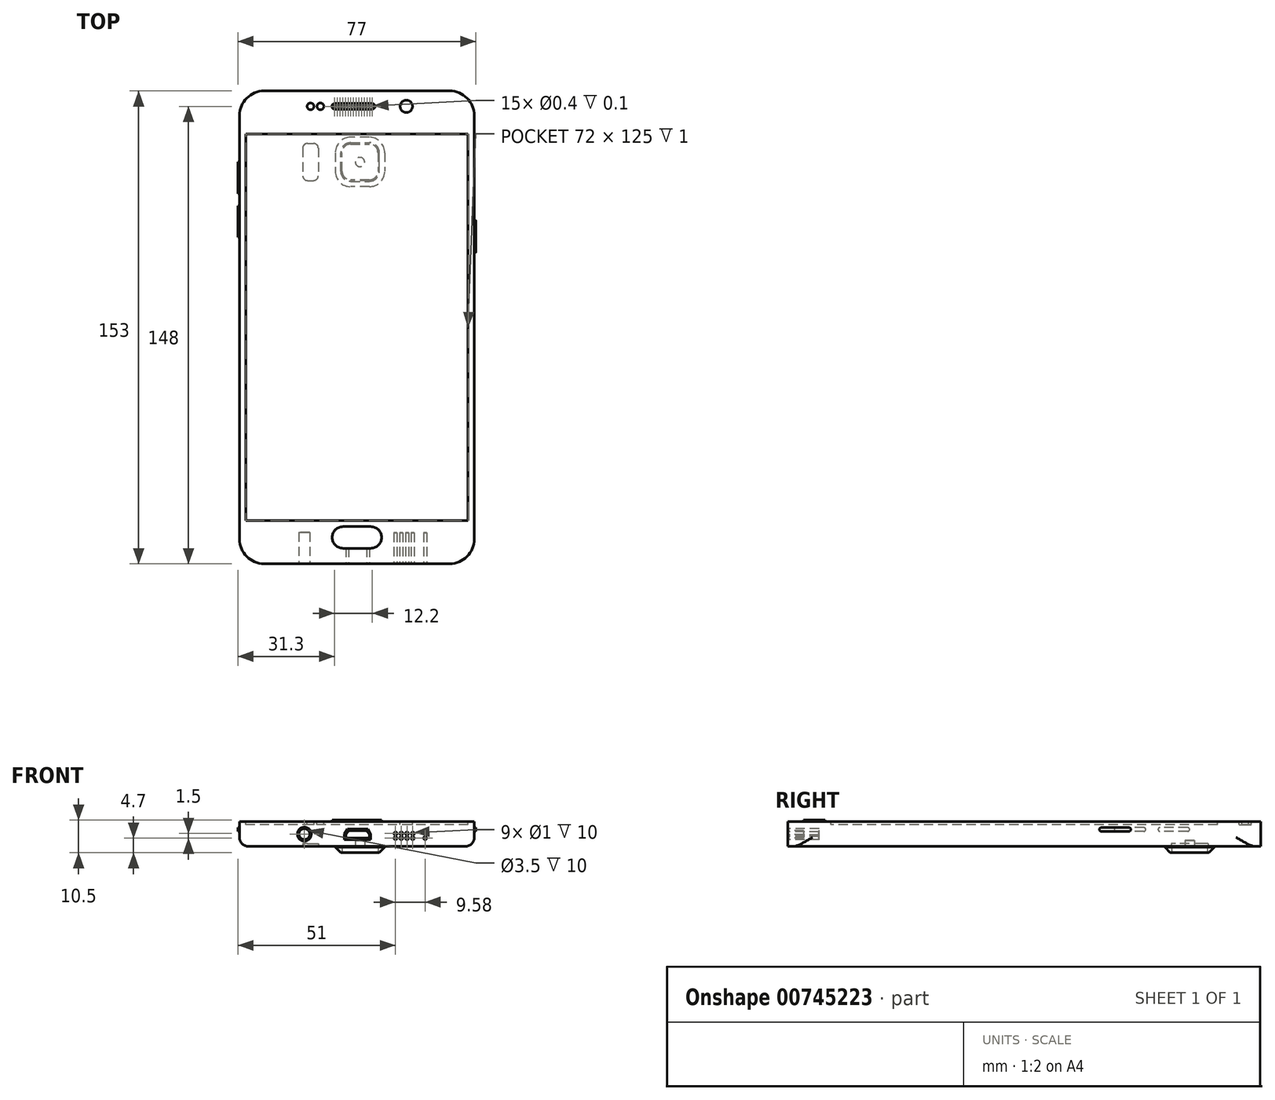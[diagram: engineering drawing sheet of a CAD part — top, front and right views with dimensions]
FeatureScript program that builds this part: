
annotation { "Feature Type Name" : "Feature", "Feature Type Description" : "" }
export const myFeature = defineFeature(function(context is Context, id is Id, definition is map)
    precondition{}
    {
        {
            var Q0;
            Q0=qCreatedBy(makeId("Top.planeOp"),FACE);
            var sketch = newSketch(context, id + "F0", { "sketchPlane" : qUnion([Q0])});
            skLineSegment(sketch, "E0.bottom", {"start": v(-38, 76.5) * mm, "end": v(38, 76.5) * mm});
            skLineSegment(sketch, "E0.top", {"start": v(-38, -76.5) * mm, "end": v(38, -76.5) * mm});
            skLineSegment(sketch, "E0.left", {"start": v(-38, 76.5) * mm, "end": v(-38, -76.5) * mm});
            skLineSegment(sketch, "E0.right", {"start": v(38, 76.5) * mm, "end": v(38, -76.5) * mm});
            skPoint(sketch, "E0.middle", {"position": v(0, 0) * mm});
            skLineSegment(sketch, "E1", {"start": v(0, 124.35) * mm, "end": v(0, -125.9) * mm, "construction": true});
            skLineSegment(sketch, "E2", {"start": v(-131.6, 0) * mm, "end": v(160.08, 0) * mm, "construction": true});
            skSolve(sketch);
        }
        {
            var Q0;
            Q0 = qSketchRegion(id + "F0", true);
            extrude(context, id + "F1", {"entities" : qUnion([Q0]), "depth" : 8 * mm, "offsetDistance" : 25 * mm});
        }
        {
            var Q0;
            Q0=makeQuery(id+"F1.opExtrude","CAP_FACE",FACE,{"disambiguationData":[OSD([sQuery(id+"F0.wireOp",EDGE,"E0.bottom"),sQuery(id+"F0.wireOp",EDGE,"E0.top"),sQuery(id+"F0.wireOp",EDGE,"E0.left"),sQuery(id+"F0.wireOp",EDGE,"E0.right")])],"isStart":false});
            var sketch = newSketch(context, id + "F2", { "sketchPlane" : qUnion([Q0])});
            skLineSegment(sketch, "E3.bottom", {"start": v(36, 62.5) * mm, "end": v(-36, 62.5) * mm});
            skLineSegment(sketch, "E3.top", {"start": v(36, -62.5) * mm, "end": v(-36, -62.5) * mm});
            skLineSegment(sketch, "E3.left", {"start": v(36, 62.5) * mm, "end": v(36, -62.5) * mm});
            skLineSegment(sketch, "E3.right", {"start": v(-36, 62.5) * mm, "end": v(-36, -62.5) * mm});
            skPoint(sketch, "E3.middle", {"position": v(0, 0) * mm});
            skSolve(sketch);
        }
        {
            var Q0;
            Q0=makeQuery(id+"F2.imprint","IMPRINT",FACE,{"disambiguationData":[TD([[makeQuery(id+"F2.imprint","IMPRINT",EDGE,{"derivedFrom":sQuery(id+"F2.wireOp",EDGE,"E3.bottom")}),1.0]])]});
            extrude(context, id + "F3", {"entities" : qUnion([Q0]), "operationType" : NewBodyOperationType.REMOVE, "oppositeDirection" : true, "depth" : 1 * mm, "offsetDistance" : 25 * mm});
        }
        {
            var Q0;
            Q0=makeQuery(id+"F1.opExtrude","CAP_FACE",FACE,{"disambiguationData":[OSD([sQuery(id+"F0.wireOp",EDGE,"E0.bottom"),sQuery(id+"F0.wireOp",EDGE,"E0.top"),sQuery(id+"F0.wireOp",EDGE,"E0.left"),sQuery(id+"F0.wireOp",EDGE,"E0.right")])],"isStart":false});
            var sketch = newSketch(context, id + "F4", { "sketchPlane" : qUnion([Q0])});
            skArc(sketch, "E4", {"start": v(-4.5, -64.5) * mm, "mid": v(-8, -68) * mm, "end": v(-4.5, -71.5) * mm});
            skArc(sketch, "E5", {"start": v(4.5, -71.5) * mm, "mid": v(8, -68) * mm, "end": v(4.5, -64.5) * mm});
            skLineSegment(sketch, "E6", {"start": v(-4.5, 87.17) * mm, "end": v(-4.5, -115.27) * mm, "construction": true});
            skLineSegment(sketch, "E7", {"start": v(4.5, 87.92) * mm, "end": v(4.5, -126.27) * mm, "construction": true});
            skLineSegment(sketch, "E8", {"start": v(-4.5, -64.5) * mm, "end": v(4.5, -64.5) * mm});
            skLineSegment(sketch, "E9", {"start": v(-4.5, -71.5) * mm, "end": v(4.5, -71.5) * mm});
            skSolve(sketch);
        }
        {
            var Q0;
            Q0 = qSketchRegion(id + "F4", true);
            extrude(context, id + "F5", {"entities" : qUnion([Q0]), "operationType" : NewBodyOperationType.ADD, "depth" : .5 * mm, "offsetDistance" : 25 * mm});
        }
        {
            var Q0;
            Q0=makeQuery(id+"F1.opExtrude","CAP_FACE",FACE,{"disambiguationData":[OSD([sQuery(id+"F0.wireOp",EDGE,"E0.bottom"),sQuery(id+"F0.wireOp",EDGE,"E0.top"),sQuery(id+"F0.wireOp",EDGE,"E0.left"),sQuery(id+"F0.wireOp",EDGE,"E0.right")])],"isStart":false});
            var sketch = newSketch(context, id + "F6", { "sketchPlane" : qUnion([Q0])});
            skCircle(sketch, "E10", {"center": v(-15, 71.5) * mm, "radius": 1.1 * mm});
            skCircle(sketch, "E11", {"center": v(-11.8, 71.5) * mm, "radius": 1.1 * mm});
            skLineSegment(sketch, "E12", {"start": v(-15, 71.5) * mm, "end": v(-11.8, 71.5) * mm, "construction": true});
            skCircle(sketch, "E13", {"center": v(16, 71.5) * mm, "radius": 2 * mm});
            skLineSegment(sketch, "E14", {"start": v(-11.8, 71.5) * mm, "end": v(16, 71.5) * mm, "construction": true});
            skSolve(sketch);
        }
        {
            var Q0;
            Q0=makeQuery(id+"F6.imprint","IMPRINT",FACE,{"disambiguationData":[TD([[makeQuery(id+"F6.imprint","IMPRINT",EDGE,{"derivedFrom":sQuery(id+"F6.wireOp",EDGE,"E10")}),1.0]])]});
            var Q1;
            Q1=makeQuery(id+"F6.imprint","IMPRINT",FACE,{"disambiguationData":[TD([[makeQuery(id+"F6.imprint","IMPRINT",EDGE,{"derivedFrom":sQuery(id+"F6.wireOp",EDGE,"E11")}),1.0]])]});
            var Q2;
            Q2=makeQuery(id+"F6.imprint","IMPRINT",FACE,{"disambiguationData":[TD([[makeQuery(id+"F6.imprint","IMPRINT",EDGE,{"derivedFrom":sQuery(id+"F6.wireOp",EDGE,"E13")}),1.0]])]});
            extrude(context, id + "F7", {"entities" : qUnion([Q0, Q1, Q2]), "operationType" : NewBodyOperationType.REMOVE, "oppositeDirection" : true, "depth" : 1 * mm, "offsetDistance" : 25 * mm});
        }
        {
            var Q0;
            Q0=makeQuery(id+"F1.opExtrude","CAP_FACE",FACE,{"disambiguationData":[OSD([sQuery(id+"F0.wireOp",EDGE,"E0.bottom"),sQuery(id+"F0.wireOp",EDGE,"E0.top"),sQuery(id+"F0.wireOp",EDGE,"E0.left"),sQuery(id+"F0.wireOp",EDGE,"E0.right")])],"isStart":false});
            var sketch = newSketch(context, id + "F8", { "sketchPlane" : qUnion([Q0])});
            skArc(sketch, "E15", {"start": v(-7.2, 72.4) * mm, "mid": v(-8.1, 71.5) * mm, "end": v(-7.2, 70.6) * mm});
            skArc(sketch, "E16", {"start": v(5, 70.6) * mm, "mid": v(5.9, 71.5) * mm, "end": v(5, 72.4) * mm});
            skLineSegment(sketch, "E17", {"start": v(-7.2, 72.4) * mm, "end": v(5, 72.4) * mm});
            skLineSegment(sketch, "E18", {"start": v(-7.2, 70.6) * mm, "end": v(5, 70.6) * mm});
            skSolve(sketch);
        }
        {
            var Q0;
            Q0 = qSketchRegion(id + "F8", true);
            extrude(context, id + "F9", {"entities" : qUnion([Q0]), "operationType" : NewBodyOperationType.ADD, "depth" : 0.01 * mm, "offsetDistance" : 25 * mm});
        }
        {
            var Q0;
            Q0=makeQuery(id+"F9.opExtrude","CAP_FACE",FACE,{"disambiguationData":[OSD([sQuery(id+"F8.wireOp",EDGE,"E15"),sQuery(id+"F8.wireOp",EDGE,"E16"),sQuery(id+"F8.wireOp",EDGE,"E17"),sQuery(id+"F8.wireOp",EDGE,"E18")])],"isStart":false});
            var sketch = newSketch(context, id + "F10", { "sketchPlane" : qUnion([Q0])});
            skLineSegment(sketch, "E19", {"start": v(-7.2, 71.5) * mm, "end": v(5, 71.5) * mm, "construction": true});
            skLineSegment(sketch, "E20", {"start": v(-1.1, 79.57) * mm, "end": v(-1.1, 67.09) * mm, "construction": true});
            skCircle(sketch, "E21", {"center": v(-1.1, 71.5) * mm, "radius": 0.2 * mm});
            skCircle(sketch, "E22", {"center": v(-7.2, 71.5) * mm, "radius": 0.2 * mm});
            skCircle(sketch, "E23", {"center": v(5, 71.5) * mm, "radius": 0.2 * mm});
            skCircle(sketch, "E24", {"center": v(-6.33, 71.5) * mm, "radius": 0.2 * mm});
            skCircle(sketch, "E25", {"center": v(-5.46, 71.5) * mm, "radius": 0.2 * mm});
            skCircle(sketch, "E26", {"center": v(-4.59, 71.5) * mm, "radius": 0.2 * mm});
            skCircle(sketch, "E27", {"center": v(-3.7, 71.5) * mm, "radius": 0.2 * mm});
            skCircle(sketch, "E28", {"center": v(-2.84, 71.5) * mm, "radius": 0.2 * mm});
            skCircle(sketch, "E29", {"center": v(-1.97, 71.5) * mm, "radius": 0.2 * mm});
            skCircle(sketch, "E30", {"center": v(-0.23, 71.5) * mm, "radius": 0.2 * mm});
            skCircle(sketch, "E31", {"center": v(0.64, 71.5) * mm, "radius": 0.2 * mm});
            skCircle(sketch, "E32", {"center": v(1.51, 71.5) * mm, "radius": 0.2 * mm});
            skCircle(sketch, "E33", {"center": v(2.39, 71.5) * mm, "radius": 0.2 * mm});
            skCircle(sketch, "E34", {"center": v(3.26, 71.5) * mm, "radius": 0.2 * mm});
            skCircle(sketch, "E35", {"center": v(4.13, 71.5) * mm, "radius": 0.2 * mm});
            skSolve(sketch);
        }
        {
            var Q0;
            Q0 = qSketchRegion(id + "F10", true);
            extrude(context, id + "F11", {"entities" : qUnion([Q0]), "operationType" : NewBodyOperationType.REMOVE, "oppositeDirection" : true, "depth" : .1 * mm, "offsetDistance" : 25 * mm});
        }
        {
            var Q0;
            Q0=makeQuery(id+"F1.opExtrude","SWEPT_FACE",FACE,{"disambiguationData":[OSD([sQuery(id+"F0.wireOp",EDGE,"E0.left")])]});
            var sketch = newSketch(context, id + "F12", { "sketchPlane" : qUnion([Q0])});
            skArc(sketch, "E36", {"start": v(-52.9, 6.1) * mm, "mid": v(-53.5, 5.5) * mm, "end": v(-52.9, 4.9) * mm});
            skArc(sketch, "E37", {"start": v(-43.9, 4.9) * mm, "mid": v(-43.3, 5.5) * mm, "end": v(-43.9, 6.1) * mm});
            skArc(sketch, "E38", {"start": v(-38.7, 6.1) * mm, "mid": v(-39.3, 5.5) * mm, "end": v(-38.7, 4.9) * mm});
            skArc(sketch, "E39", {"start": v(-29.7, 4.9) * mm, "mid": v(-29.1, 5.5) * mm, "end": v(-29.7, 6.1) * mm});
            skLineSegment(sketch, "E40", {"start": v(-52.9, 5.5) * mm, "end": v(-29.7, 5.5) * mm, "construction": true});
            skLineSegment(sketch, "E41", {"start": v(-52.9, 6.1) * mm, "end": v(-43.9, 6.1) * mm});
            skLineSegment(sketch, "E42", {"start": v(-52.9, 4.9) * mm, "end": v(-43.9, 4.9) * mm});
            skLineSegment(sketch, "E43.trimOffspring", {"start": v(-38.7, 6.1) * mm, "end": v(-29.7, 6.1) * mm});
            skLineSegment(sketch, "E44.trimOffspring", {"start": v(-38.7, 4.9) * mm, "end": v(-29.7, 4.9) * mm});
            skSolve(sketch);
        }
        {
            var Q0;
            Q0 = qSketchRegion(id + "F12", true);
            extrude(context, id + "F13", {"entities" : qUnion([Q0]), "operationType" : NewBodyOperationType.ADD, "depth" : .5 * mm, "offsetDistance" : 25 * mm});
        }
        {
            var Q0;
            Q0=makeQuery(id+"F1.opExtrude","SWEPT_FACE",FACE,{"disambiguationData":[OSD([sQuery(id+"F0.wireOp",EDGE,"E0.right")])]});
            var sketch = newSketch(context, id + "F14", { "sketchPlane" : qUnion([Q0])});
            skCircle(sketch, "E45", {"center": v(24.9, 5.5) * mm, "radius": 0.6 * mm});
            skCircle(sketch, "E46", {"center": v(33.9, 5.5) * mm, "radius": 0.6 * mm});
            skLineSegment(sketch, "E47", {"start": v(24.9, 6.1) * mm, "end": v(33.9, 6.1) * mm});
            skLineSegment(sketch, "E48", {"start": v(24.9, 4.9) * mm, "end": v(33.9, 4.9) * mm});
            skLineSegment(sketch, "E49", {"start": v(24.9, 5.5) * mm, "end": v(33.9, 5.5) * mm, "construction": true});
            skSolve(sketch);
        }
        {
            var Q0;
            Q0 = qSketchRegion(id + "F14", true);
            extrude(context, id + "F15", {"entities" : qUnion([Q0]), "operationType" : NewBodyOperationType.ADD, "depth" : .5 * mm, "offsetDistance" : 25 * mm});
        }
        {
            var Q0;
            Q0=makeQuery(id+"F1.opExtrude","SWEPT_FACE",FACE,{"disambiguationData":[OSD([sQuery(id+"F0.wireOp",EDGE,"E0.top")])]});
            var sketch = newSketch(context, id + "F16", { "sketchPlane" : qUnion([Q0])});
            skCircle(sketch, "E50", {"center": v(-17, 4) * mm, "radius": 2.25 * mm});
            skSolve(sketch);
        }
        {
            var Q0;
            Q0 = qSketchRegion(id + "F16", true);
            extrude(context, id + "F17", {"entities" : qUnion([Q0]), "operationType" : NewBodyOperationType.REMOVE, "oppositeDirection" : true, "depth" : .1 * mm, "offsetDistance" : 25 * mm});
        }
        {
            var Q0;
            Q0=makeQuery(id+"F17.boolean.opBoolean","COPY",FACE,{"derivedFrom":makeQuery(id+"F17.opExtrude","CAP_FACE",FACE,{"disambiguationData":[OSD([sQuery(id+"F16.wireOp",EDGE,"E50")])],"isStart":false})});
            var sketch = newSketch(context, id + "F18", { "sketchPlane" : qUnion([Q0])});
            skCircle(sketch, "E51", {"center": v(-17, 4) * mm, "radius": 1.75 * mm});
            skSolve(sketch);
        }
        {
            var Q0;
            Q0 = qSketchRegion(id + "F18", true);
            extrude(context, id + "F19", {"entities" : qUnion([Q0]), "operationType" : NewBodyOperationType.REMOVE, "oppositeDirection" : true, "depth" : 10 * mm, "offsetDistance" : 25 * mm});
        }
        {
            var Q0;
            Q0=makeQuery(id+"F1.opExtrude","SWEPT_FACE",FACE,{"disambiguationData":[OSD([sQuery(id+"F0.wireOp",EDGE,"E0.top")])]});
            var sketch = newSketch(context, id + "F20", { "sketchPlane" : qUnion([Q0])});
            skLineSegment(sketch, "E52", {"start": v(0.25, -5.5) * mm, "end": v(0.25, -17.35) * mm, "construction": true});
            skLineSegment(sketch, "E53", {"start": v(0.25, 5.6) * mm, "end": v(3.5, 5.6) * mm});
            skLineSegment(sketch, "E54", {"start": v(3.5, 5.6) * mm, "end": v(4.5, 4) * mm});
            skLineSegment(sketch, "E55", {"start": v(4.5, 4) * mm, "end": v(4.5, 2.2) * mm});
            skLineSegment(sketch, "E56", {"start": v(4.5, 2.2) * mm, "end": v(0.25, 2.2) * mm});
            skLineSegment(sketch, "E57.MirrorCS", {"start": v(-4, 2.2) * mm, "end": v(0.25, 2.2) * mm});
            skLineSegment(sketch, "E58.MirrorCS", {"start": v(-4, 4) * mm, "end": v(-4, 2.2) * mm});
            skLineSegment(sketch, "E59.MirrorCS", {"start": v(-3, 5.6) * mm, "end": v(-4, 4) * mm});
            skLineSegment(sketch, "E60.MirrorCS", {"start": v(0.25, 5.6) * mm, "end": v(-3, 5.6) * mm});
            skLineSegment(sketch, "E61", {"start": v(-4, 4) * mm, "end": v(36.69, 4) * mm, "construction": true});
            skSolve(sketch);
        }
        {
            var Q0;
            Q0 = qSketchRegion(id + "F20", true);
            extrude(context, id + "F21", {"entities" : qUnion([Q0]), "operationType" : NewBodyOperationType.REMOVE, "oppositeDirection" : true, "depth" : .1 * mm, "offsetDistance" : 25 * mm});
        }
        {
            var Q0;
            Q0=makeQuery(id+"F21.boolean.opBoolean","COPY",FACE,{"derivedFrom":makeQuery(id+"F21.opExtrude","CAP_FACE",FACE,{"disambiguationData":[OSD([sQuery(id+"F20.wireOp",EDGE,"E53"),sQuery(id+"F20.wireOp",EDGE,"E54"),sQuery(id+"F20.wireOp",EDGE,"E55"),sQuery(id+"F20.wireOp",EDGE,"E56"),sQuery(id+"F20.wireOp",EDGE,"E57.MirrorCS"),sQuery(id+"F20.wireOp",EDGE,"E58.MirrorCS"),sQuery(id+"F20.wireOp",EDGE,"E59.MirrorCS"),sQuery(id+"F20.wireOp",EDGE,"E60.MirrorCS")])],"isStart":false})});
            var sketch = newSketch(context, id + "F22", { "sketchPlane" : qUnion([Q0])});
            skLineSegment(sketch, "E62", {"start": v(0.25, 7.04) * mm, "end": v(0.25, -1.36) * mm, "construction": true});
            skPoint(sketch, "E62.startSnap0", {"position": v(0.25, 5.6) * mm});
            skLineSegment(sketch, "E63", {"start": v(0.25, 5.1) * mm, "end": v(3.22, 5.1) * mm});
            skLineSegment(sketch, "E64", {"start": v(3.22, 5.1) * mm, "end": v(4, 3.86) * mm});
            skLineSegment(sketch, "E65", {"start": v(4, 3.86) * mm, "end": v(4, 2.7) * mm});
            skLineSegment(sketch, "E66", {"start": v(4, 2.7) * mm, "end": v(0.25, 2.7) * mm});
            skLineSegment(sketch, "E67.MirrorCS", {"start": v(-3.5, 2.7) * mm, "end": v(0.25, 2.7) * mm});
            skLineSegment(sketch, "E68.MirrorCS", {"start": v(0.25, 5.1) * mm, "end": v(-2.72, 5.1) * mm});
            skLineSegment(sketch, "E69.MirrorCS", {"start": v(-2.72, 5.1) * mm, "end": v(-3.5, 3.86) * mm});
            skLineSegment(sketch, "E70.MirrorCS", {"start": v(-3.5, 3.86) * mm, "end": v(-3.5, 2.7) * mm});
            skSolve(sketch);
        }
        {
            var Q0;
            Q0 = qSketchRegion(id + "F22", true);
            extrude(context, id + "F23", {"entities" : qUnion([Q0]), "operationType" : NewBodyOperationType.REMOVE, "oppositeDirection" : true, "depth" : 5 * mm, "offsetDistance" : 25 * mm});
        }
        {
            var Q0;
            Q0=makeQuery(id+"F1.opExtrude","SWEPT_FACE",FACE,{"disambiguationData":[OSD([sQuery(id+"F0.wireOp",EDGE,"E0.top")])]});
            var sketch = newSketch(context, id + "F24", { "sketchPlane" : qUnion([Q0])});
            skLineSegment(sketch, "E71", {"start": v(44.86, 3.45) * mm, "end": v(6.77, 3.45) * mm, "construction": true});
            skLineSegment(sketch, "E72", {"start": v(12.5, 10.5) * mm, "end": v(12.5, -4.17) * mm, "construction": true});
            skLineSegment(sketch, "E73.0", {"start": v(44.86, 4.2) * mm, "end": v(6.77, 4.2) * mm, "construction": true});
            skLineSegment(sketch, "E74.0", {"start": v(44.86, 2.7) * mm, "end": v(6.77, 2.7) * mm, "construction": true});
            skLineSegment(sketch, "E75.0", {"start": v(-43, -5) * mm, "end": v(43, -5) * mm, "construction": true});
            skLineSegment(sketch, "E75.1", {"start": v(-43, 13) * mm, "end": v(-43, -5) * mm, "construction": true});
            skLineSegment(sketch, "E75.2", {"start": v(43, 13) * mm, "end": v(-43, 13) * mm, "construction": true});
            skLineSegment(sketch, "E75.3", {"start": v(43, -5) * mm, "end": v(43, 13) * mm, "construction": true});
            skLineSegment(sketch, "E76.0", {"start": v(14.36, 10.5) * mm, "end": v(14.36, -4.17) * mm, "construction": true});
            skLineSegment(sketch, "E77.0", {"start": v(16.22, 10.5) * mm, "end": v(16.22, -4.17) * mm, "construction": true});
            skLineSegment(sketch, "E78.0", {"start": v(18.08, 10.5) * mm, "end": v(18.08, -4.17) * mm, "construction": true});
            skCircle(sketch, "E79", {"center": v(12.5, 4.2) * mm, "radius": 0.5 * mm});
            skCircle(sketch, "E80", {"center": v(14.36, 4.2) * mm, "radius": 0.5 * mm});
            skCircle(sketch, "E81", {"center": v(16.22, 4.2) * mm, "radius": 0.5 * mm});
            skCircle(sketch, "E82", {"center": v(18.08, 4.2) * mm, "radius": 0.5 * mm});
            skCircle(sketch, "E83", {"center": v(18.08, 2.7) * mm, "radius": 0.5 * mm});
            skCircle(sketch, "E84", {"center": v(16.22, 2.7) * mm, "radius": 0.5 * mm});
            skCircle(sketch, "E85", {"center": v(14.36, 2.7) * mm, "radius": 0.5 * mm});
            skCircle(sketch, "E86", {"center": v(12.5, 2.7) * mm, "radius": 0.5 * mm});
            skLineSegment(sketch, "E87", {"start": v(22.08, 10.5) * mm, "end": v(22.08, -2.74) * mm, "construction": true});
            skCircle(sketch, "E88", {"center": v(22.08, 2.7) * mm, "radius": 0.5 * mm});
            skSolve(sketch);
        }
        {
            var Q0;
            Q0 = qSketchRegion(id + "F24", true);
            extrude(context, id + "F25", {"entities" : qUnion([Q0]), "operationType" : NewBodyOperationType.REMOVE, "oppositeDirection" : true, "depth" : 10 * mm, "offsetDistance" : 25 * mm});
        }
        {
            var Q0;
            Q0=makeQuery(id+"F1.opExtrude","CAP_FACE",FACE,{"disambiguationData":[OSD([sQuery(id+"F0.wireOp",EDGE,"E0.bottom"),sQuery(id+"F0.wireOp",EDGE,"E0.top"),sQuery(id+"F0.wireOp",EDGE,"E0.left"),sQuery(id+"F0.wireOp",EDGE,"E0.right")])],"isStart":true});
            var sketch = newSketch(context, id + "F26", { "sketchPlane" : qUnion([Q0])});
            skLineSegment(sketch, "E89.bottom", {"start": v(4, -61.5) * mm, "end": v(-2, -61.5) * mm});
            skLineSegment(sketch, "E89.top", {"start": v(4, -45.5) * mm, "end": v(-2, -45.5) * mm});
            skLineSegment(sketch, "E89.left", {"start": v(9, -56.5) * mm, "end": v(9, -50.5) * mm});
            skLineSegment(sketch, "E89.right", {"start": v(-7, -56.5) * mm, "end": v(-7, -50.5) * mm});
            skPoint(sketch, "E90.visualSharp", {"position": v(-7, -61.5) * mm});
            skArc(sketch, "E90.filletArc", {"start": v(-7, -56.5) * mm, "mid": v(-5.54, -60.04) * mm, "end": v(-2, -61.5) * mm});
            skPoint(sketch, "E91.visualSharp", {"position": v(9, -45.5) * mm});
            skArc(sketch, "E91.filletArc", {"start": v(9, -50.5) * mm, "mid": v(7.54, -46.96) * mm, "end": v(4, -45.5) * mm});
            skPoint(sketch, "E92.visualSharp", {"position": v(9, -61.5) * mm});
            skArc(sketch, "E92.filletArc", {"start": v(4, -61.5) * mm, "mid": v(7.54, -60.04) * mm, "end": v(9, -56.5) * mm});
            skPoint(sketch, "E93.visualSharp", {"position": v(-7, -45.5) * mm});
            skArc(sketch, "E93.filletArc", {"start": v(-2, -45.5) * mm, "mid": v(-5.54, -46.96) * mm, "end": v(-7, -50.5) * mm});
            skSolve(sketch);
        }
        {
            var Q0;
            Q0 = qSketchRegion(id + "F26", true);
            extrude(context, id + "F27", {"entities" : qUnion([Q0]), "operationType" : NewBodyOperationType.ADD, "depth" : 2 * mm, "offsetDistance" : 25 * mm});
        }
        {
            var Q0;
            Q0=makeQuery(id+"F27.opExtrude","CAP_EDGE",EDGE,{"disambiguationData":[OSD([sQuery(id+"F26.wireOp",EDGE,"E89.left")])],"isStart":false});
            chamfer(context, id + "F28", {"entities" : qUnion([Q0]), "width" : 1.8 * mm, "tangentPropagation" : true});
        }
        {
            var Q0;
            {var subQ0=sQuery(id+"F26.wireOp",EDGE,"E92.filletArc");Q0=makeQuery(id+"F28.opChamfer","BLEND_EDGE",EDGE,{"blendedFrom":[makeQuery(id+"F27.opExtrude","CAP_EDGE",EDGE,{"disambiguationData":[OSD([subQ0])],"isStart":false}),makeQuery(id+"F27.opExtrude","CAP_FACE",FACE,{"disambiguationData":[OSD([sQuery(id+"F26.wireOp",EDGE,"E89.bottom"),sQuery(id+"F26.wireOp",EDGE,"E89.top"),sQuery(id+"F26.wireOp",EDGE,"E89.left"),sQuery(id+"F26.wireOp",EDGE,"E89.right"),sQuery(id+"F26.wireOp",EDGE,"E90.filletArc"),sQuery(id+"F26.wireOp",EDGE,"E91.filletArc"),subQ0,sQuery(id+"F26.wireOp",EDGE,"E93.filletArc")])],"isStart":false})],"blendedInto":[makeQuery(id+"F27.opExtrude","CAP_FACE",FACE,{"disambiguationData":[OSD([sQuery(id+"F26.wireOp",EDGE,"E89.bottom"),sQuery(id+"F26.wireOp",EDGE,"E89.top"),sQuery(id+"F26.wireOp",EDGE,"E89.left"),sQuery(id+"F26.wireOp",EDGE,"E89.right"),sQuery(id+"F26.wireOp",EDGE,"E90.filletArc"),sQuery(id+"F26.wireOp",EDGE,"E91.filletArc"),subQ0,sQuery(id+"F26.wireOp",EDGE,"E93.filletArc")])],"isStart":false})]});}
            chamfer(context, id + "F29", {"entities" : qUnion([Q0]), "width" : 0.2 * mm, "tangentPropagation" : true});
        }
        {
            var Q0;
            Q0=makeQuery(id+"F27.opExtrude","CAP_FACE",FACE,{"disambiguationData":[OSD([sQuery(id+"F26.wireOp",EDGE,"E89.bottom"),sQuery(id+"F26.wireOp",EDGE,"E89.top"),sQuery(id+"F26.wireOp",EDGE,"E89.left"),sQuery(id+"F26.wireOp",EDGE,"E89.right"),sQuery(id+"F26.wireOp",EDGE,"E90.filletArc"),sQuery(id+"F26.wireOp",EDGE,"E91.filletArc"),sQuery(id+"F26.wireOp",EDGE,"E92.filletArc"),sQuery(id+"F26.wireOp",EDGE,"E93.filletArc")])],"isStart":false});
            var sketch = newSketch(context, id + "F30", { "sketchPlane" : qUnion([Q0])});
            skArc(sketch, "E94.0", {"start": v(-4.8, -56.5) * mm, "mid": v(-3.98, -58.48) * mm, "end": v(-2, -59.3) * mm});
            skLineSegment(sketch, "E94.1", {"start": v(-4.8, -50.5) * mm, "end": v(-4.8, -56.5) * mm});
            skLineSegment(sketch, "E94.2", {"start": v(-2, -59.3) * mm, "end": v(4, -59.3) * mm});
            skArc(sketch, "E94.3", {"start": v(-2, -47.7) * mm, "mid": v(-3.98, -48.52) * mm, "end": v(-4.8, -50.5) * mm});
            skArc(sketch, "E94.4", {"start": v(4, -59.3) * mm, "mid": v(5.98, -58.48) * mm, "end": v(6.8, -56.5) * mm});
            skLineSegment(sketch, "E94.5", {"start": v(6.8, -56.5) * mm, "end": v(6.8, -50.5) * mm});
            skArc(sketch, "E94.6", {"start": v(6.8, -50.5) * mm, "mid": v(5.98, -48.52) * mm, "end": v(4, -47.7) * mm});
            skLineSegment(sketch, "E94.7", {"start": v(4, -47.7) * mm, "end": v(-2, -47.7) * mm});
            skSolve(sketch);
        }
        {
            var Q0;
            Q0 = qSketchRegion(id + "F30", true);
            extrude(context, id + "F31", {"entities" : qUnion([Q0]), "operationType" : NewBodyOperationType.REMOVE, "oppositeDirection" : true, "depth" : 2 * mm, "offsetDistance" : 25 * mm});
        }
        {
            var Q0;
            Q0=makeQuery(id+"F31.boolean.opBoolean","COPY",FACE,{"derivedFrom":makeQuery(id+"F31.opExtrude","CAP_FACE",FACE,{"disambiguationData":[OSD([sQuery(id+"F30.wireOp",EDGE,"E94.0"),sQuery(id+"F30.wireOp",EDGE,"E94.1"),sQuery(id+"F30.wireOp",EDGE,"E94.2"),sQuery(id+"F30.wireOp",EDGE,"E94.3"),sQuery(id+"F30.wireOp",EDGE,"E94.4"),sQuery(id+"F30.wireOp",EDGE,"E94.5"),sQuery(id+"F30.wireOp",EDGE,"E94.6"),sQuery(id+"F30.wireOp",EDGE,"E94.7")])],"isStart":false})});
            var sketch = newSketch(context, id + "F32", { "sketchPlane" : qUnion([Q0])});
            skLineSegment(sketch, "E95", {"start": v(1, -59.3) * mm, "end": v(1, -47.7) * mm, "construction": true});
            skLineSegment(sketch, "E96", {"start": v(6.8, -53.5) * mm, "end": v(-4.8, -53.5) * mm, "construction": true});
            skCircle(sketch, "E97", {"center": v(1, -53.5) * mm, "radius": 1.5 * mm});
            skSolve(sketch);
        }
        {
            var Q0;
            Q0 = qSketchRegion(id + "F32", true);
            extrude(context, id + "F33", {"entities" : qUnion([Q0]), "operationType" : NewBodyOperationType.REMOVE, "oppositeDirection" : true, "depth" : 2 * mm, "offsetDistance" : 25 * mm});
        }
        {
            var Q0;
            Q0=makeQuery(id+"F1.opExtrude","CAP_FACE",FACE,{"disambiguationData":[OSD([sQuery(id+"F0.wireOp",EDGE,"E0.bottom"),sQuery(id+"F0.wireOp",EDGE,"E0.top"),sQuery(id+"F0.wireOp",EDGE,"E0.left"),sQuery(id+"F0.wireOp",EDGE,"E0.right")])],"isStart":true});
            var sketch = newSketch(context, id + "F34", { "sketchPlane" : qUnion([Q0])});
            skLineSegment(sketch, "E98", {"start": v(9, -53.5) * mm, "end": v(-43.1, -53.5) * mm, "construction": true});
            skLineSegment(sketch, "E99", {"start": v(-15, -78.99) * mm, "end": v(-15, -36.79) * mm, "construction": true});
            skLineSegment(sketch, "E100", {"start": v(-38, -70.47) * mm, "end": v(-38, -82.04) * mm, "construction": true});
            skLineSegment(sketch, "E101.bottom", {"start": v(-16, -59.5) * mm, "end": v(-14, -59.5) * mm});
            skLineSegment(sketch, "E101.top", {"start": v(-16, -47.5) * mm, "end": v(-14, -47.5) * mm});
            skLineSegment(sketch, "E101.left", {"start": v(-17.5, -58) * mm, "end": v(-17.5, -49) * mm});
            skLineSegment(sketch, "E101.right", {"start": v(-12.5, -58) * mm, "end": v(-12.5, -49) * mm});
            skPoint(sketch, "E101.middle", {"position": v(-15, -53.5) * mm});
            skPoint(sketch, "E102.visualSharp", {"position": v(-12.5, -59.5) * mm});
            skArc(sketch, "E102.filletArc", {"start": v(-14, -59.5) * mm, "mid": v(-12.94, -59.06) * mm, "end": v(-12.5, -58) * mm});
            skPoint(sketch, "E103.visualSharp", {"position": v(-17.5, -59.5) * mm});
            skArc(sketch, "E103.filletArc", {"start": v(-17.5, -58) * mm, "mid": v(-17.06, -59.06) * mm, "end": v(-16, -59.5) * mm});
            skPoint(sketch, "E104.visualSharp", {"position": v(-12.5, -47.5) * mm});
            skArc(sketch, "E104.filletArc", {"start": v(-12.5, -49) * mm, "mid": v(-12.94, -47.94) * mm, "end": v(-14, -47.5) * mm});
            skPoint(sketch, "E105.visualSharp", {"position": v(-17.5, -47.5) * mm});
            skArc(sketch, "E105.filletArc", {"start": v(-16, -47.5) * mm, "mid": v(-17.06, -47.94) * mm, "end": v(-17.5, -49) * mm});
            skSolve(sketch);
        }
        {
            var Q0;
            Q0 = qSketchRegion(id + "F34", true);
            extrude(context, id + "F35", {"entities" : qUnion([Q0]), "operationType" : NewBodyOperationType.REMOVE, "oppositeDirection" : true, "depth" : 1 * mm, "offsetDistance" : 25 * mm});
        }
        {
            var Q0;
            Q0=makeQuery(id+"F1.opExtrude","SWEPT_EDGE",EDGE,{"disambiguationData":[OSD([sQuery(id+"F0.wireOp",EDGE,"E0.bottom"),sQuery(id+"F0.wireOp",EDGE,"E0.right")])]});
            var Q1;
            Q1=makeQuery(id+"F1.opExtrude","SWEPT_EDGE",EDGE,{"disambiguationData":[OSD([sQuery(id+"F0.wireOp",EDGE,"E0.bottom"),sQuery(id+"F0.wireOp",EDGE,"E0.left")])]});
            var Q2;
            Q2=makeQuery(id+"F1.opExtrude","SWEPT_EDGE",EDGE,{"disambiguationData":[OSD([sQuery(id+"F0.wireOp",EDGE,"E0.top"),sQuery(id+"F0.wireOp",EDGE,"E0.left")])]});
            var Q3;
            Q3=makeQuery(id+"F1.opExtrude","SWEPT_EDGE",EDGE,{"disambiguationData":[OSD([sQuery(id+"F0.wireOp",EDGE,"E0.top"),sQuery(id+"F0.wireOp",EDGE,"E0.right")])]});
            fillet(context, id + "F36", {"entities" : qUnion([Q0, Q1, Q2, Q3]), "radius" : 8 * mm, "tangentPropagation" : true, "allowEdgeOverflow" : false});
        }
        {
            var Q0;
            Q0=makeQuery(id+"F1.opExtrude","CAP_EDGE",EDGE,{"disambiguationData":[OSD([sQuery(id+"F0.wireOp",EDGE,"E0.right")])],"isStart":true});
            var Q1;
            Q1=makeQuery(id+"F1.opExtrude","CAP_EDGE",EDGE,{"disambiguationData":[OSD([sQuery(id+"F0.wireOp",EDGE,"E0.left")])],"isStart":true});
            fillet(context, id + "F37", {"entities" : qUnion([Q0, Q1]), "radius" : 3 * mm, "allowEdgeOverflow" : false});
        }
    });
